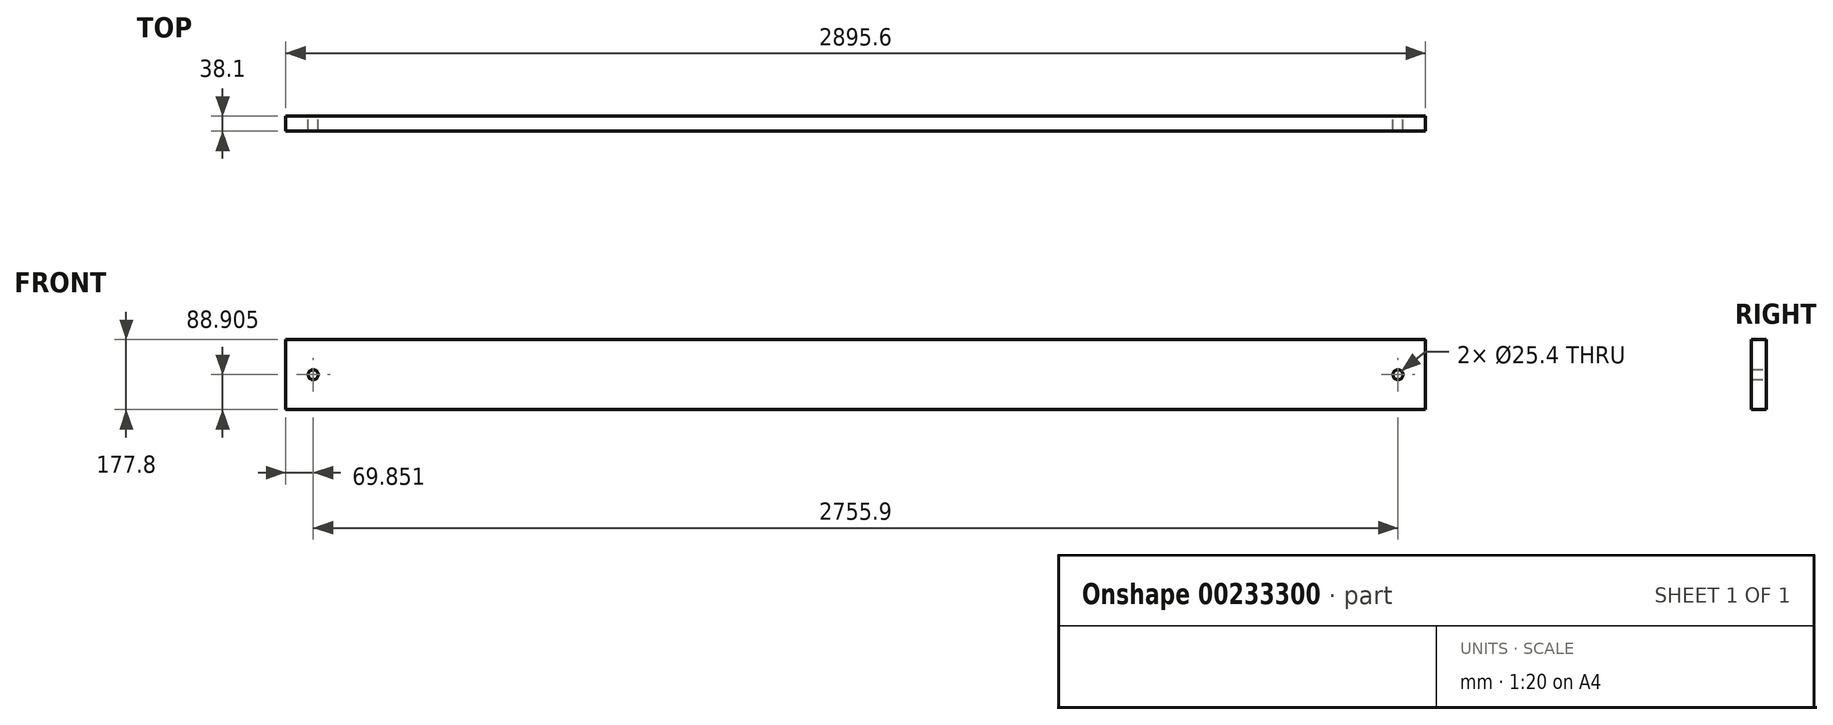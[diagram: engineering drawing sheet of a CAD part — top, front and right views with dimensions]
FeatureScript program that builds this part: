
annotation { "Feature Type Name" : "Feature", "Feature Type Description" : "" }
export const myFeature = defineFeature(function(context is Context, id is Id, definition is map)
    precondition{}
    {
        {
            var Q0;
            Q0=qCreatedBy(makeId("Front.planeOp"),FACE);
            var sketch = newSketch(context, id + "F0", { "sketchPlane" : qUnion([Q0])});
            skLineSegment(sketch, "E0.bottom", {"start": v(-1445.1, -435.67) * mm, "end": v(1450.5, -435.67) * mm});
            skLineSegment(sketch, "E0.top", {"start": v(-1445.1, -613.47) * mm, "end": v(1450.5, -613.47) * mm});
            skLineSegment(sketch, "E0.left", {"start": v(-1445.1, -435.67) * mm, "end": v(-1445.1, -613.47) * mm});
            skLineSegment(sketch, "E0.right", {"start": v(1450.5, -435.67) * mm, "end": v(1450.5, -613.47) * mm});
            skCircle(sketch, "E1", {"center": v(-1375.25, -524.57) * mm, "radius": 12.7 * mm});
            skCircle(sketch, "E2", {"center": v(1380.65, -524.57) * mm, "radius": 12.7 * mm});
            skSolve(sketch);
        }
        {
            var Q0;
            Q0 = qSketchRegion(id + "F0", true);
            extrude(context, id + "F1", {"entities" : qUnion([Q0]), "depth" : 38.1 * mm});
        }
    });
